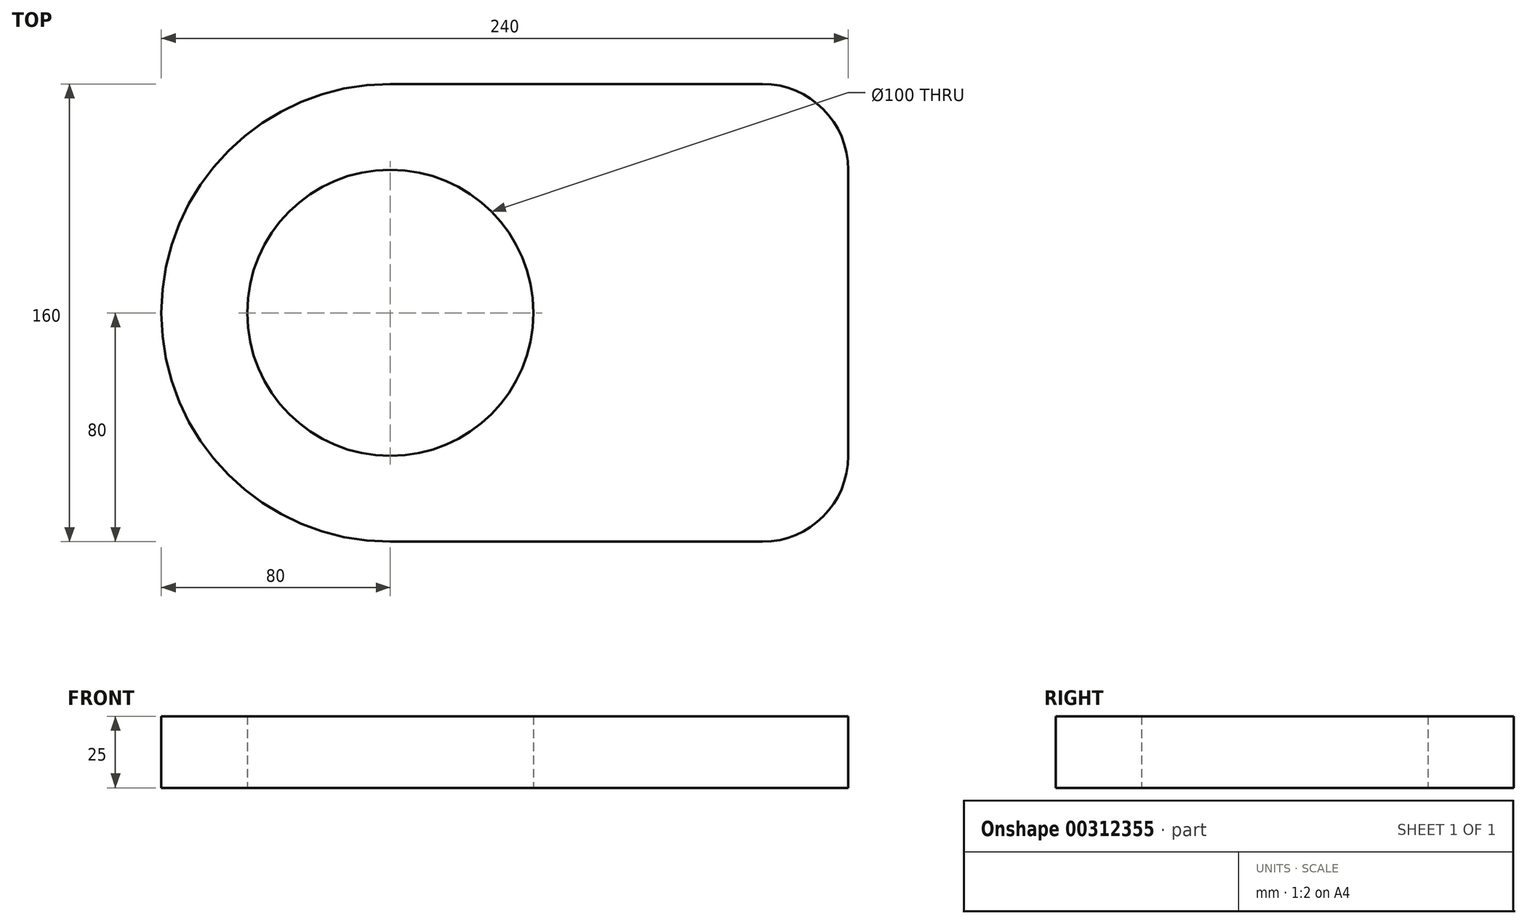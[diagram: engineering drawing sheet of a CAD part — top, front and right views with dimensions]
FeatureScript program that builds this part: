
annotation { "Feature Type Name" : "Feature", "Feature Type Description" : "" }
export const myFeature = defineFeature(function(context is Context, id is Id, definition is map)
    precondition{}
    {
        {
            var Q0;
            Q0=qCreatedBy(makeId("Top.planeOp"),FACE);
            var sketch = newSketch(context, id + "F0", { "sketchPlane" : qUnion([Q0])});
            skArc(sketch, "E0", {"start": v(0, 80) * mm, "mid": v(-80, 0) * mm, "end": v(0, -80) * mm});
            skLineSegment(sketch, "E1", {"start": v(0, 80) * mm, "end": v(130, 80) * mm});
            skLineSegment(sketch, "E2", {"start": v(0, -80) * mm, "end": v(130, -80) * mm});
            skLineSegment(sketch, "E3", {"start": v(160, -50) * mm, "end": v(160, 50) * mm});
            skCircle(sketch, "E4", {"center": v(0, 0) * mm, "radius": 50 * mm});
            skPoint(sketch, "E5.visualSharp", {"position": v(160, 80) * mm});
            skArc(sketch, "E5.filletArc", {"start": v(160, 50) * mm, "mid": v(151.21, 71.21) * mm, "end": v(130, 80) * mm});
            skPoint(sketch, "E6.visualSharp", {"position": v(160, -80) * mm});
            skArc(sketch, "E6.filletArc", {"start": v(130, -80) * mm, "mid": v(151.21, -71.21) * mm, "end": v(160, -50) * mm});
            skSolve(sketch);
        }
        {
            var Q0;
            Q0 = qSketchRegion(id + "F0", true);
            extrude(context, id + "F1", {"entities" : qUnion([Q0]), "depth" : 25 * mm});
        }
    });
